# Revit family: Cumberland-Celina-Lounge1
name_source: partatom
category: Furniture
revit_build: Autodesk Revit 2014 (Build: 20130308_1515(x64)
units: mm (PartAtom-declared; Revit-internal decimal feet)

## types (6) — shared parameters
Assembly Code = E2020200
Back Finish = CUM - Linen - Beige
Depth = 30 1/16"
Height = 29"
Keynote = 12500
Leg = CUM - OAK
Low Emitting Finish = Yes
Low Emitting Material = Yes
Manufacturer = Cumberland
Panel Finish = CUM - OAK
Salvage or Reuse = Yes
Seat = CUM - Linen - Beige
Type Comments = Celina
URL = www.cumberlandfurniture.com
Wood Panel = CUM - OAK
zero-valued in all types: Percentage of Recycled Content

## per-type parameters (varying)
| type | Back Dist | Cut | Cut v | Description | Uph | Width | Wood |
| 2650 | 33" | 1/8" | No | Celina 32"W 29"H 30"D | Yes | 33" | No |
| 2653 | 33" | 1/4" | No | Celina 32"W 29"H 30"D, Wood Panel | No | 33" | Yes |
| 2654 | 57" | 35" | Yes | Celina 57"W 29"H 30"D, Wood Panel | No | 57" | Yes |
| 2655 | 78" | 35" | Yes | Celina 78"W 29"H 30"D, Wood Panel | No | 78" | Yes |
| 2651 | 57" | 35" | Yes | Celina 57"W 29"H 30"D | Yes | 57" | No |
| 2652 | 78" | 35" | Yes | Celina 78"W 29"H 30"D | Yes | 78" | No |

note: column(s) folded — value = type name in every type: Model

## geometry (parser evidence)
native form markers: Sweep x7
no freeform markers — native parametric forms only
